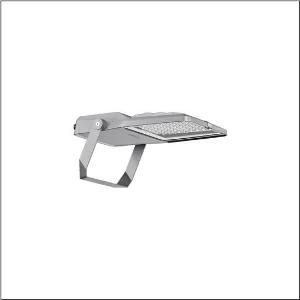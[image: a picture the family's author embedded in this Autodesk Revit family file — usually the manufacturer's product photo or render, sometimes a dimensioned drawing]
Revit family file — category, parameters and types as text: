
# Revit family: floodlight_fl_21_iq_mini___pl61_5xa7772c5c1a_22e4
name_source: partatom
category: Lighting Fixtures
units: mm (PartAtom-declared; Revit-internal decimal feet)

## family parameters
Cut with Voids When Loaded = No
Host = Face
Light Source = No
Part Type = Normal
Room Calculation Point = No
Round Connector Dimension = Use Diameter
Shared = No

## types (1)
- --- (1 x LED, 11180 lm, 87.2 W, 4000K)
    Apparent Load = 87 VA
    CIE Flux Codes = 33 65 98 100 100
    Color Rendering = 80
    Color Temperature = 4000K
    Default Elevation = 1800 mm
    Description = Floodlight FL 21 iQ mini, floodlight, primary light control with lens, of PMMA, primary optical cover: protective disc, of toughened safety glass, transparent, light distribution: PL61, light emission: direct distribution, installation type: surface-mounted, lamps: LED, High Power LED, rated values: 11.180lm | 87,2W | 128,2lm/W (begin service life); end service life: 11.180lm | 92,1W; at 50% lumin. flux: 5.590lm | 40,1W | 139,4lm/W, colour temperature: 4000K, colour rendering: CRI > 80, light colour: 840, light setting 1 begin service life: 100% | 11.180lm | 87,2W | 128,2lm/W | 4.000K, light setting 1 end service life: 92,1W, further light settings possible, control: Street-Remote, Auto-Match, Temp-Guard, Night-Set, Smart-Wire, Desk-Remote (wireless, voltage-free reading and setting of iQ features in the workshop via application-optimized NFC function/RFID function), optimised constant luminous flux control (CLO 2.0), pre-setting: linear dimming characteristic, with terminal, 6-pole, mains connection: 220..240V, AC, 50/60Hz, luminaire housing, of diecast aluminium, powder-coated, SITECO metallic grey (DB 702S), corrosivity category C5 mid according to DIN EN ISO 12944suitable for swimming poolschlorine-resistant, sealing non-destructively replaceable, mounting bracket, of steel, galvanised, powder-coated, SITECO metallic grey (DB 702S), protection rating (complete): IP66, insulation class (complete): insulation class II (safety insulation), certification: CE, ENEC, VDE, protection symbol: D, impact resistance: IK08, permissible operating ambient temperature: -40..+40°C, permissible operating ambient temperature for outdoor applications: -40..+50°C, standard: DIN EN 12944, LABS conformity tested according to VDMA 24364:2018-05, packaging unit: 1 piece

Light Distribution: PL61
    Height = 70 mm
    Lamp = 1 x LED
    Lamp Light Flux = 11180 lm
    Lamp Power = 87.2 W
    Lamp count = 1
    Length = 485 mm
    Luminous efficacy = 128 lm/W
    Manufacturer = Siteco
    ModVariant = No
    Model = 5XA7772C5C1A
    Mounting Place = Pole
    Mounting Type = Pole annexe
    Number of Poles = 1
    OnlyDefault = Yes
    Power Factor = 1
    Product Name = Floodlight FL 21 iQ mini | PL61
    Product group = floodlight | pylon annexe
    ProductGroupID = 6201
    Protection Class = Protection class II
    Protection Degree = IP 66
    RLX_Detail_Level = 1
    RLX_Emergency_Light_Flux = 0 lm
    RLX_Emergency_Type = 0
    RLX_Emergency_Type_DB = No
    RlxData = <blob elided: 96657 chars, md5=29d3741a>
    Socket = socket
    Standby Power = 0 W
    System Light Flux = 11180 lm
    System Power = 87 W
    Type Comments = factory setting: luminous flux: 100 % | dim-lin: 254 | 456 mA
    Type Image = l_1006845.jpg
    URL = http://relux.com
    VarID = @adj_173905
    Voltage = 0 V
    Weight = 0.00 kg
    Width = 337 mm

## geometry (parser evidence)
native form markers: Blend x4, Sweep x14
no freeform markers — native parametric forms only
